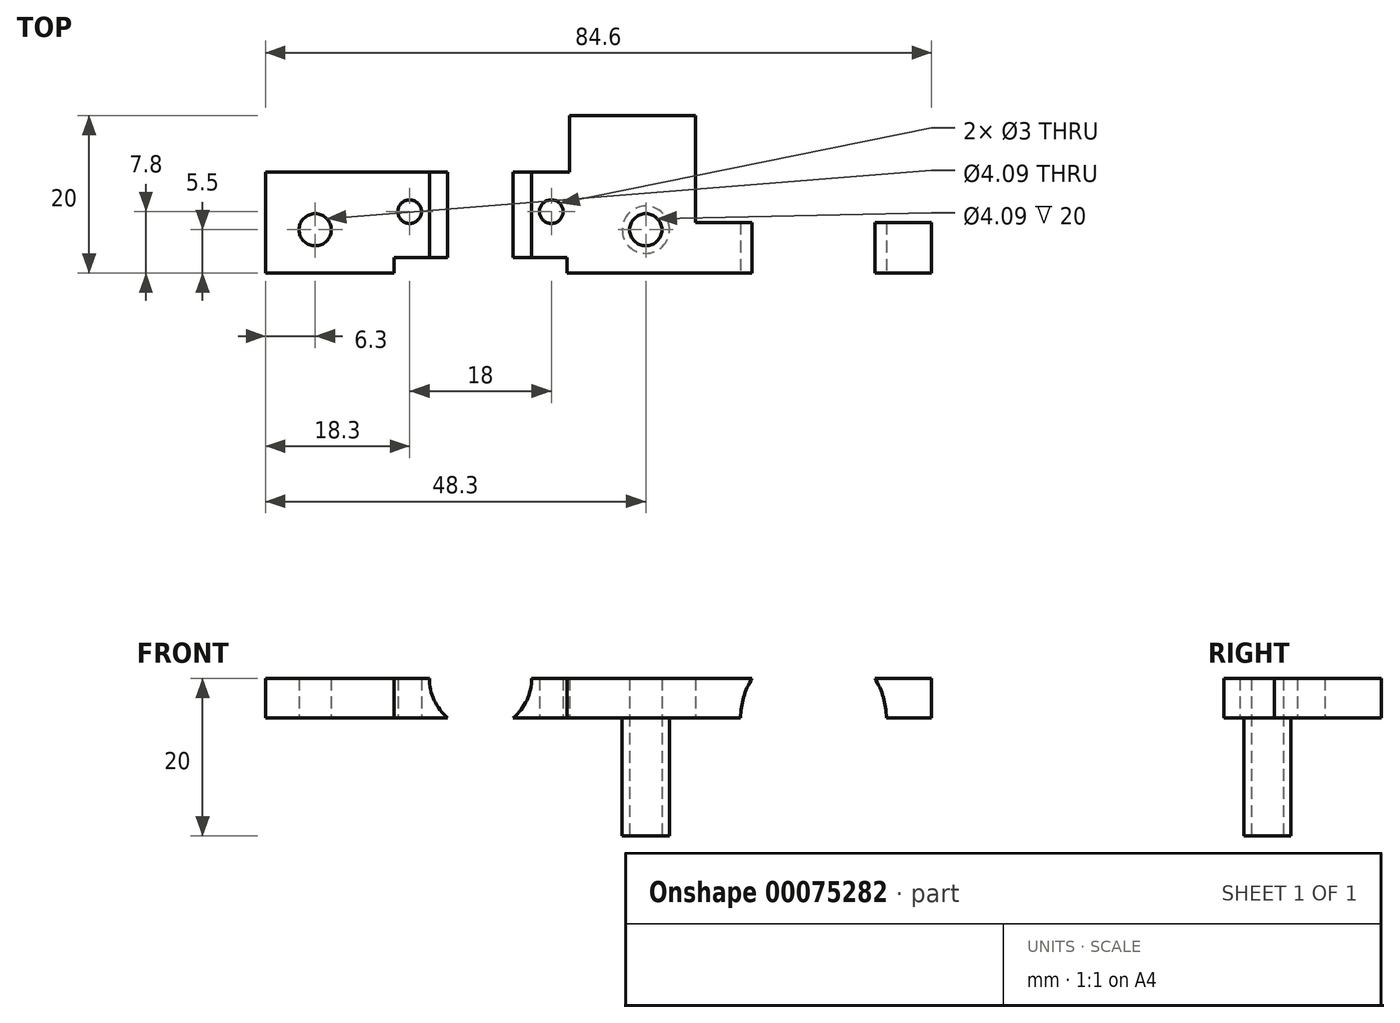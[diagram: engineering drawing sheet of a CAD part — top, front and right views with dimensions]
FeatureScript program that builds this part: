
annotation { "Feature Type Name" : "Feature", "Feature Type Description" : "" }
export const myFeature = defineFeature(function(context is Context, id is Id, definition is map)
    precondition{}
    {
        {
            var Q0;
            Q0=qCreatedBy(makeId("Top.planeOp"),FACE);
            var sketch = newSketch(context, id + "F0", { "sketchPlane" : qUnion([Q0])});
            skLineSegment(sketch, "E0.rect.bottom", {"start": v(-27.3, 6.4) * mm, "end": v(27.3, 6.4) * mm, "construction": true});
            skLineSegment(sketch, "E0.rect.top", {"start": v(-27.3, -6.4) * mm, "end": v(27.3, -6.4) * mm, "construction": true});
            skLineSegment(sketch, "E0.rect.left", {"start": v(-27.3, 6.4) * mm, "end": v(-27.3, -6.4) * mm, "construction": true});
            skLineSegment(sketch, "E0.rect.right", {"start": v(27.3, 6.4) * mm, "end": v(27.3, -6.4) * mm, "construction": true});
            skPoint(sketch, "E0.rect.middle", {"position": v(0, 0) * mm});
            skLineSegment(sketch, "E1", {"start": v(0, 6.4) * mm, "end": v(-27.3, 6.4) * mm});
            skCircle(sketch, "E2", {"center": v(-9, 1.4) * mm, "radius": 1.5 * mm});
            skCircle(sketch, "E3.MirrorC", {"center": v(9, 1.4) * mm, "radius": 1.5 * mm});
            skLineSegment(sketch, "E4", {"start": v(-11, 6.4) * mm, "end": v(-11, -6.4) * mm, "construction": true});
            skLineSegment(sketch, "E5", {"start": v(0, -4.4) * mm, "end": v(-11, -4.4) * mm});
            skLineSegment(sketch, "E6", {"start": v(-11, -4.4) * mm, "end": v(-11, -6.4) * mm});
            skLineSegment(sketch, "E7", {"start": v(-27.3, -6.4) * mm, "end": v(-27.3, 6.4) * mm});
            skLineSegment(sketch, "E8", {"start": v(-27.3, -6.4) * mm, "end": v(-11, -6.4) * mm});
            skLineSegment(sketch, "E9.MirrorCS", {"start": v(11, 6.4) * mm, "end": v(11, -6.4) * mm, "construction": true});
            skLineSegment(sketch, "E10", {"start": v(0, -4.4) * mm, "end": v(11, -4.4) * mm});
            skLineSegment(sketch, "E11", {"start": v(11, -4.4) * mm, "end": v(11, -6.4) * mm});
            skLineSegment(sketch, "E12", {"start": v(11, -6.4) * mm, "end": v(27.3, -6.4) * mm});
            skCircle(sketch, "E13", {"center": v(-21, -0.9) * mm, "radius": 2.05 * mm});
            skCircle(sketch, "E14.MirrorC", {"center": v(21, -0.9) * mm, "radius": 2.05 * mm});
            skLineSegment(sketch, "E15", {"start": v(27.3, -6.4) * mm, "end": v(27.3, 13.6) * mm});
            skPoint(sketch, "E15.endSnap0", {"position": v(27.3, 0) * mm});
            skLineSegment(sketch, "E16", {"start": v(27.3, 13.6) * mm, "end": v(11.3, 13.6) * mm});
            skLineSegment(sketch, "E17", {"start": v(11.3, 13.6) * mm, "end": v(11.3, 6.4) * mm});
            skLineSegment(sketch, "E18", {"start": v(11.3, 6.4) * mm, "end": v(0, 6.4) * mm});
            skLineSegment(sketch, "E19", {"start": v(27.3, -6.4) * mm, "end": v(57.3, -6.4) * mm});
            skLineSegment(sketch, "E20", {"start": v(57.3, -6.4) * mm, "end": v(57.3, 0) * mm});
            skLineSegment(sketch, "E21", {"start": v(57.3, 0) * mm, "end": v(27.3, 0) * mm});
            skSolve(sketch);
        }
        {
            var Q0;
            Q0=makeQuery(id+"F0.imprint","IMPRINT",FACE,{"disambiguationData":[TD([[makeQuery(id+"F0.imprint","IMPRINT",EDGE,{"derivedFrom":sQuery(id+"F0.wireOp",EDGE,"E1")}),1.0]])]});
            extrude(context, id + "F1", {"entities" : qUnion([Q0]), "depth" : 20 * mm});
        }
        {
            var Q0;
            {var subQ0=sQuery(id+"F0.wireOp",EDGE,"E19");Q0=makeQuery(id+"F0.imprint","IMPRINT",FACE,{"disambiguationData":[TD([[makeQuery(id+"F0.imprint","IMPRINT",EDGE,{"derivedFrom":subQ0}),1.0]])]});}
            extrude(context, id + "F2", {"entities" : qUnion([Q0]), "operationType" : NewBodyOperationType.ADD, "depth" : 30 * mm});
        }
        {
            var Q0;
            Q0=makeQuery(id+"F1.opExtrude","SWEPT_FACE",FACE,{"disambiguationData":[OSD([sQuery(id+"F0.wireOp",EDGE,"E5"),sQuery(id+"F0.wireOp",EDGE,"E10")])]});
            var sketch = newSketch(context, id + "F3", { "sketchPlane" : qUnion([Q0])});
            skCircle(sketch, "E22", {"center": v(0, 20) * mm, "radius": 6.5 * mm});
            skSolve(sketch);
        }
        {
            var Q0;
            Q0 = qSketchRegion(id + "F3", true);
            extrude(context, id + "F4", {"entities" : qUnion([Q0]), "operationType" : NewBodyOperationType.REMOVE, "endBound" : BoundingType.THROUGH_ALL, "oppositeDirection" : true, "depth" : 25 * mm});
        }
        {
            var Q0;
            Q0=makeQuery(id+"F1.opExtrude","CAP_FACE",FACE,{"disambiguationData":[OSD([sQuery(id+"F0.wireOp",EDGE,"E1"),sQuery(id+"F0.wireOp",EDGE,"E2"),sQuery(id+"F0.wireOp",EDGE,"E3.MirrorC"),sQuery(id+"F0.wireOp",EDGE,"E5"),sQuery(id+"F0.wireOp",EDGE,"E6"),sQuery(id+"F0.wireOp",EDGE,"E7"),sQuery(id+"F0.wireOp",EDGE,"E8"),sQuery(id+"F0.wireOp",EDGE,"E10"),sQuery(id+"F0.wireOp",EDGE,"E11"),sQuery(id+"F0.wireOp",EDGE,"E12"),sQuery(id+"F0.wireOp",EDGE,"E13"),sQuery(id+"F0.wireOp",EDGE,"E14.MirrorC"),sQuery(id+"F0.wireOp",EDGE,"E15"),sQuery(id+"F0.wireOp",EDGE,"E16"),sQuery(id+"F0.wireOp",EDGE,"E17"),sQuery(id+"F0.wireOp",EDGE,"E18")])],"isStart":true});
            var sketch = newSketch(context, id + "F5", { "sketchPlane" : qUnion([Q0])});
            skCircle(sketch, "E23", {"center": v(-21, 0.9) * mm, "radius": 3 * mm});
            skCircle(sketch, "E24.MirrorC", {"center": v(21, 0.9) * mm, "radius": 3 * mm});
            skSolve(sketch);
        }
        {
            var Q0;
            Q0=makeQuery(id+"F5.imprint","IMPRINT",FACE,{"disambiguationData":[TD([[makeQuery(id+"F5.imprint","IMPRINT",EDGE,{"derivedFrom":sQuery(id+"F5.wireOp",EDGE,"E23")}),1.0]])]});
            var Q1;
            Q1=makeQuery(id+"F5.imprint","IMPRINT",FACE,{"disambiguationData":[TD([[makeQuery(id+"F5.imprint","IMPRINT",EDGE,{"derivedFrom":sQuery(id+"F5.wireOp",EDGE,"E24.MirrorC")}),-1.0]])]});
            extrude(context, id + "F6", {"entities" : qUnion([Q0, Q1]), "operationType" : NewBodyOperationType.REMOVE, "oppositeDirection" : true, "depth" : 15 * mm});
        }
        {
            var Q0;
            Q0=makeQuery(id+"F2.boolean.opBoolean","MERGE",FACE,{"derivedFrom":[makeQuery(id+"F1.opExtrude","SWEPT_FACE",FACE,{"disambiguationData":[OSD([sQuery(id+"F0.wireOp",EDGE,"E12")])]}),makeQuery(id+"F2.opExtrude","SWEPT_FACE",FACE,{"disambiguationData":[OSD([sQuery(id+"F0.wireOp",EDGE,"E19")])]})]});
            var sketch = newSketch(context, id + "F7", { "sketchPlane" : qUnion([Q0])});
            skLineSegment(sketch, "E25", {"start": v(27.3, 30) * mm, "end": v(57.3, 0) * mm, "construction": true});
            skCircle(sketch, "E26", {"center": v(42.3, 15) * mm, "radius": 9.25 * mm});
            skSolve(sketch);
        }
        {
            var Q0;
            Q0=makeQuery(id+"F7.imprint","IMPRINT",FACE,{"disambiguationData":[TD([[makeQuery(id+"F7.imprint","IMPRINT",EDGE,{"derivedFrom":sQuery(id+"F7.wireOp",EDGE,"E26")}),1.0]])]});
            extrude(context, id + "F8", {"entities" : qUnion([Q0]), "operationType" : NewBodyOperationType.REMOVE, "endBound" : BoundingType.THROUGH_ALL, "oppositeDirection" : true, "depth" : 25 * mm});
        }
        {
            var Q0;
            Q0=makeQuery(id+"F2.opExtrude","CAP_FACE",FACE,{"disambiguationData":[OSD([sQuery(id+"F0.wireOp",EDGE,"E15"),sQuery(id+"F0.wireOp",EDGE,"E19"),sQuery(id+"F0.wireOp",EDGE,"E20"),sQuery(id+"F0.wireOp",EDGE,"E21")])],"isStart":false});
            extrude(context, id + "F9", {"entities" : qUnion([Q0]), "operationType" : NewBodyOperationType.REMOVE, "oppositeDirection" : true, "depth" : 10 * mm});
        }
        {
            var Q0;
            Q0=makeQuery(id+"F0.imprint","IMPRINT",FACE,{"disambiguationData":[TD([[makeQuery(id+"F0.imprint","IMPRINT",EDGE,{"derivedFrom":sQuery(id+"F0.wireOp",EDGE,"E1")}),1.0]])]});
            var sketch = newSketch(context, id + "F10", { "sketchPlane" : qUnion([Q0])});
            skCircle(sketch, "E27.cCircle", {"center": v(9, 1.4) * mm, "radius": 3 * mm, "construction": true});
            skLineSegment(sketch, "E27.0", {"start": v(10.5, 4) * mm, "end": v(12, 1.4) * mm});
            skLineSegment(sketch, "E27.1", {"start": v(12, 1.4) * mm, "end": v(10.5, -1.2) * mm});
            skLineSegment(sketch, "E27.2", {"start": v(10.5, -1.2) * mm, "end": v(7.5, -1.2) * mm});
            skLineSegment(sketch, "E27.3", {"start": v(7.5, -1.2) * mm, "end": v(6, 1.4) * mm});
            skLineSegment(sketch, "E27.4", {"start": v(6, 1.4) * mm, "end": v(7.5, 4) * mm});
            skLineSegment(sketch, "E27.5", {"start": v(7.5, 4) * mm, "end": v(10.5, 4) * mm});
            skLineSegment(sketch, "E28.MirrorCS", {"start": v(-7.5, -1.2) * mm, "end": v(-6, 1.4) * mm});
            skLineSegment(sketch, "E29.MirrorCS", {"start": v(-10.5, -1.2) * mm, "end": v(-7.5, -1.2) * mm});
            skLineSegment(sketch, "E30.MirrorCS", {"start": v(-12, 1.4) * mm, "end": v(-10.5, -1.2) * mm});
            skLineSegment(sketch, "E31.MirrorCS", {"start": v(-10.5, 4) * mm, "end": v(-12, 1.4) * mm});
            skLineSegment(sketch, "E32.MirrorCS", {"start": v(-7.5, 4) * mm, "end": v(-10.5, 4) * mm});
            skLineSegment(sketch, "E33.MirrorCS", {"start": v(-6, 1.4) * mm, "end": v(-7.5, 4) * mm});
            skSolve(sketch);
        }
        {
            var Q0;
            Q0 = qSketchRegion(id + "F10", true);
            extrude(context, id + "F11", {"entities" : qUnion([Q0]), "operationType" : NewBodyOperationType.REMOVE, "depth" : 3 * mm});
        }
    });
